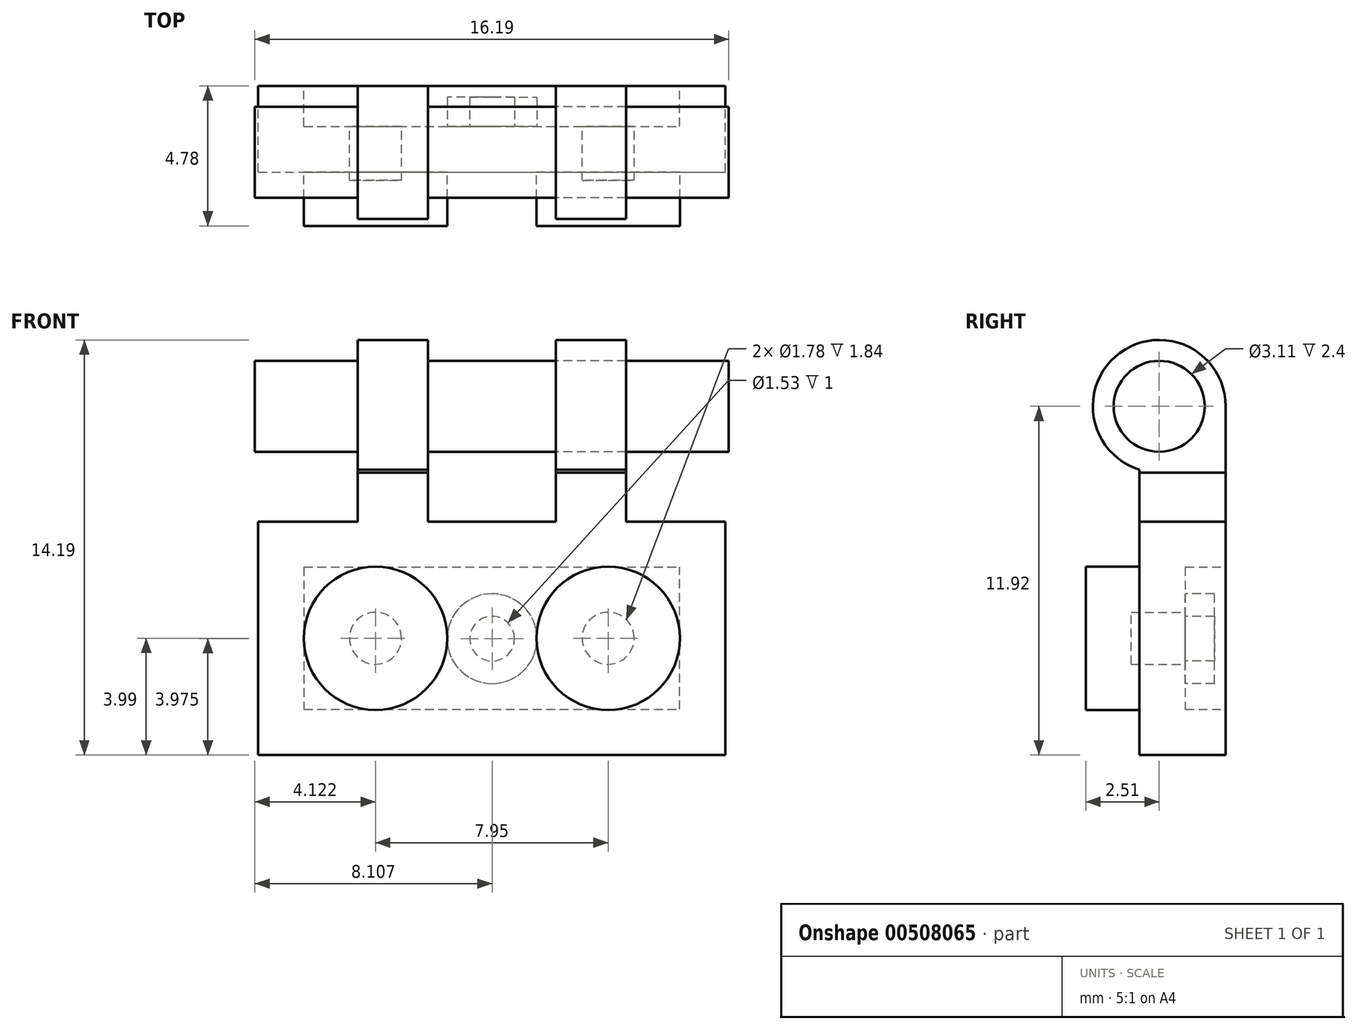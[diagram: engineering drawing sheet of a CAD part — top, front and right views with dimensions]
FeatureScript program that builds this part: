
annotation { "Feature Type Name" : "Feature", "Feature Type Description" : "" }
export const myFeature = defineFeature(function(context is Context, id is Id, definition is map)
    precondition{}
    {
        {
            var Q0;
            Q0=qCreatedBy(makeId("Front.planeOp"),FACE);
            var sketch = newSketch(context, id + "F0", { "sketchPlane" : qUnion([Q0])});
            skLineSegment(sketch, "E0", {"start": v(-14.86, 22.42) * mm, "end": v(1.1, 22.42) * mm});
            skLineSegment(sketch, "E1", {"start": v(-14.86, 22.42) * mm, "end": v(-14.86, 14.44) * mm});
            skLineSegment(sketch, "E2", {"start": v(-14.86, 14.44) * mm, "end": v(1.1, 14.44) * mm});
            skLineSegment(sketch, "E3", {"start": v(1.1, 14.44) * mm, "end": v(1.1, 22.42) * mm});
            skSolve(sketch);
        }
        {
            var Q0;
            Q0 = qSketchRegion(id + "F0", true);
            extrude(context, id + "F1", {"entities" : qUnion([Q0]), "depth" : 2.94 * mm});
        }
        {
            var Q0;
            Q0=makeQuery(id+"F1.opExtrude","CAP_FACE",FACE,{"disambiguationData":[OSD([sQuery(id+"F0.wireOp",EDGE,"E0"),sQuery(id+"F0.wireOp",EDGE,"E1"),sQuery(id+"F0.wireOp",EDGE,"E2"),sQuery(id+"F0.wireOp",EDGE,"E3")])],"isStart":false});
            var sketch = newSketch(context, id + "F2", { "sketchPlane" : qUnion([Q0])});
            skCircle(sketch, "E4", {"center": v(-10.86, 18.43) * mm, "radius": 2.45 * mm});
            skCircle(sketch, "E5", {"center": v(-2.9, 18.43) * mm, "radius": 2.45 * mm});
            skSolve(sketch);
        }
        {
            var Q0;
            Q0 = qSketchRegion(id + "F2", true);
            extrude(context, id + "F3", {"entities" : qUnion([Q0]), "operationType" : NewBodyOperationType.ADD, "depth" : 1.84 * mm});
        }
        {
            var Q0;
            Q0=makeQuery(id+"F1.opExtrude","CAP_FACE",FACE,{"disambiguationData":[OSD([sQuery(id+"F0.wireOp",EDGE,"E0"),sQuery(id+"F0.wireOp",EDGE,"E1"),sQuery(id+"F0.wireOp",EDGE,"E2"),sQuery(id+"F0.wireOp",EDGE,"E3")])],"isStart":true});
            shell(context, id + "F4", {"entities" : qUnion([Q0]), "thickness" : 1.56 * mm});
        }
        {
            var Q0;
            Q0=makeQuery(id+"F4.opShell","OFFSET_FACE",FACE,{"disambiguationData":[OSD([sQuery(id+"F0.wireOp",EDGE,"E0"),sQuery(id+"F0.wireOp",EDGE,"E1"),sQuery(id+"F0.wireOp",EDGE,"E2"),sQuery(id+"F0.wireOp",EDGE,"E3")])]});
            var sketch = newSketch(context, id + "F5", { "sketchPlane" : qUnion([Q0])});
            skCircle(sketch, "E6", {"center": v(6.87, 18.41) * mm, "radius": 1.53 * mm});
            skCircle(sketch, "E7", {"center": v(6.87, 18.41) * mm, "radius": 0.77 * mm});
            skSolve(sketch);
        }
        {
            var Q0;
            Q0 = qSketchRegion(id + "F5", true);
            extrude(context, id + "F6", {"entities" : qUnion([Q0]), "operationType" : NewBodyOperationType.ADD, "depth" : 1 * mm, "offsetDistance" : 25 * mm});
        }
        {
            var Q0;
            Q0=makeQuery(id+"F1.opExtrude","SWEPT_FACE",FACE,{"disambiguationData":[OSD([sQuery(id+"F0.wireOp",EDGE,"E0")])]});
            var sketch = newSketch(context, id + "F7", { "sketchPlane" : qUnion([Q0])});
            skLineSegment(sketch, "E8", {"start": v(-6.88, -2.94) * mm, "end": v(-6.88, 0) * mm});
            skLineSegment(sketch, "E9", {"start": v(-6.88, -1.47) * mm, "end": v(-9.07, -1.47) * mm});
            skPoint(sketch, "E9.endSnap0", {"position": v(-6.88, -1.47) * mm});
            skLineSegment(sketch, "E10", {"start": v(-6.88, -1.47) * mm, "end": v(-4.7, -1.47) * mm});
            skLineSegment(sketch, "E11", {"start": v(-4.7, -2.94) * mm, "end": v(-4.7, 0) * mm});
            skLineSegment(sketch, "E12", {"start": v(-9.07, -2.94) * mm, "end": v(-9.07, 0) * mm});
            skLineSegment(sketch, "E13", {"start": v(-2.3, -2.94) * mm, "end": v(-2.3, 0) * mm});
            skLineSegment(sketch, "E14", {"start": v(-11.47, -2.94) * mm, "end": v(-11.47, 0) * mm});
            skLineSegment(sketch, "E15", {"start": v(-2.3, -2.94) * mm, "end": v(-4.7, -2.94) * mm});
            skLineSegment(sketch, "E16", {"start": v(-2.3, 0) * mm, "end": v(-4.7, 0) * mm});
            skLineSegment(sketch, "E17", {"start": v(-9.07, -2.94) * mm, "end": v(-11.47, -2.94) * mm});
            skLineSegment(sketch, "E18", {"start": v(-9.07, 0) * mm, "end": v(-11.47, 0) * mm});
            skSolve(sketch);
        }
        {
            var Q0;
            Q0 = qSketchRegion(id + "F7", true);
            extrude(context, id + "F8", {"entities" : qUnion([Q0]), "operationType" : NewBodyOperationType.ADD, "depth" : 1.67 * mm, "offsetDistance" : 25 * mm});
        }
        {
            var Q0;
            Q0=makeQuery(id+"F8.opExtrude","SWEPT_FACE",FACE,{"disambiguationData":[OSD([sQuery(id+"F7.wireOp",EDGE,"E13")])]});
            var sketch = newSketch(context, id + "F9", { "sketchPlane" : qUnion([Q0])});
            skLineSegment(sketch, "E19", {"start": v(0, 24.09) * mm, "end": v(-2.27, 24.09) * mm});
            skLineSegment(sketch, "E20", {"start": v(-2.27, 24.09) * mm, "end": v(-2.27, 26.36) * mm});
            skCircle(sketch, "E21", {"center": v(-2.27, 26.36) * mm, "radius": 2.27 * mm});
            skLineSegment(sketch, "E22", {"start": v(-2.94, 24.09) * mm, "end": v(-2.94, 24.2) * mm});
            skLineSegment(sketch, "E23", {"start": v(0, 24.09) * mm, "end": v(0, 26.36) * mm});
            skCircle(sketch, "E24", {"center": v(-2.27, 26.36) * mm, "radius": 1.55 * mm});
            skSolve(sketch);
        }
        {
            var Q0;
            Q0 = qSketchRegion(id + "F9", true);
            var Q1;
            {var subQ4=sQuery(id+"F9.wireOp",EDGE,"E22");Q1=makeQuery(id+"F9.imprint","IMPRINT",FACE,{"disambiguationData":[TD([[makeQuery(id+"F9.imprint","IMPRINT",EDGE,{"derivedFrom":subQ4}),-1.0]])]});}
            extrude(context, id + "F10", {"entities" : qUnion([Q0, Q1]), "oppositeDirection" : true, "depth" : 2.4 * mm});
        }
        {
            var Q0;
            Q0=makeQuery(id+"F8.opExtrude","SWEPT_FACE",FACE,{"disambiguationData":[OSD([sQuery(id+"F7.wireOp",EDGE,"E14")])]});
            var sketch = newSketch(context, id + "F11", { "sketchPlane" : qUnion([Q0])});
            skLineSegment(sketch, "E25", {"start": v(0, 24.09) * mm, "end": v(2.27, 24.09) * mm});
            skLineSegment(sketch, "E26", {"start": v(2.27, 24.09) * mm, "end": v(2.27, 26.36) * mm});
            skCircle(sketch, "E27", {"center": v(2.27, 26.36) * mm, "radius": 2.27 * mm});
            skLineSegment(sketch, "E28", {"start": v(2.94, 24.09) * mm, "end": v(2.94, 24.2) * mm});
            skLineSegment(sketch, "E29", {"start": v(0, 24.09) * mm, "end": v(0, 26.36) * mm});
            skSolve(sketch);
        }
        {
            var Q0;
            {var subQ0=sQuery(id+"F11.wireOp",EDGE,"E27");var subQ3=makeQuery(id+"F11.imprint","INTERSECT",VERTEX,{"derivedFrom":[subQ0,sQuery(id+"F11.wireOp",EDGE,"E28")]});Q0=makeQuery(id+"F11.imprint","IMPRINT",FACE,{"disambiguationData":[TD([[makeQuery(id+"F11.imprint","IMPRINT",EDGE,{"disambiguationData":[TD([[subQ3,-1.0]])],"derivedFrom":subQ0}),1.0]])]});}
            var Q1;
            {var subQ4=sQuery(id+"F11.wireOp",EDGE,"E28");Q1=makeQuery(id+"F11.imprint","IMPRINT",FACE,{"disambiguationData":[TD([[makeQuery(id+"F11.imprint","IMPRINT",EDGE,{"derivedFrom":subQ4}),1.0]])]});}
            var Q2;
            {var subQ0=sQuery(id+"F11.wireOp",EDGE,"E25");Q2=makeQuery(id+"F11.imprint","IMPRINT",FACE,{"disambiguationData":[TD([[makeQuery(id+"F11.imprint","IMPRINT",EDGE,{"derivedFrom":subQ0}),-1.0]])]});}
            extrude(context, id + "F12", {"entities" : qUnion([Q0, Q1, Q2]), "oppositeDirection" : true, "depth" : 2.4 * mm, "offsetDistance" : 25 * mm});
        }
        {
            var Q0;
            Q0=makeQuery(id+"F12.opExtrude","CAP_FACE",FACE,{"disambiguationData":[OSD([sQuery(id+"F7.wireOp",EDGE,"E14"),sQuery(id+"F11.wireOp",EDGE,"E25"),sQuery(id+"F11.wireOp",EDGE,"E27"),sQuery(id+"F11.wireOp",EDGE,"E28"),sQuery(id+"F11.wireOp",EDGE,"E29")])],"isStart":false});
            var sketch = newSketch(context, id + "F13", { "sketchPlane" : qUnion([Q0])});
            skCircle(sketch, "E30", {"center": v(-2.27, 26.36) * mm, "radius": 1.55 * mm});
            skSolve(sketch);
        }
        {
            var Q0;
            Q0 = qSketchRegion(id + "F13", true);
            extrude(context, id + "F14", {"entities" : qUnion([Q0]), "depth" : 10.28 * mm});
        }
        {
            var Q0;
            Q0=makeQuery(id+"F12.opExtrude","CAP_FACE",FACE,{"disambiguationData":[OSD([sQuery(id+"F7.wireOp",EDGE,"E14"),sQuery(id+"F11.wireOp",EDGE,"E25"),sQuery(id+"F11.wireOp",EDGE,"E27"),sQuery(id+"F11.wireOp",EDGE,"E28"),sQuery(id+"F11.wireOp",EDGE,"E29")])],"isStart":true});
            var sketch = newSketch(context, id + "F15", { "sketchPlane" : qUnion([Q0])});
            skCircle(sketch, "E31", {"center": v(2.27, 26.36) * mm, "radius": 1.55 * mm});
            skSolve(sketch);
        }
        {
            var Q0;
            Q0 = qSketchRegion(id + "F15", true);
            extrude(context, id + "F16", {"entities" : qUnion([Q0]), "operationType" : NewBodyOperationType.ADD, "depth" : 3.5 * mm});
        }
    });
